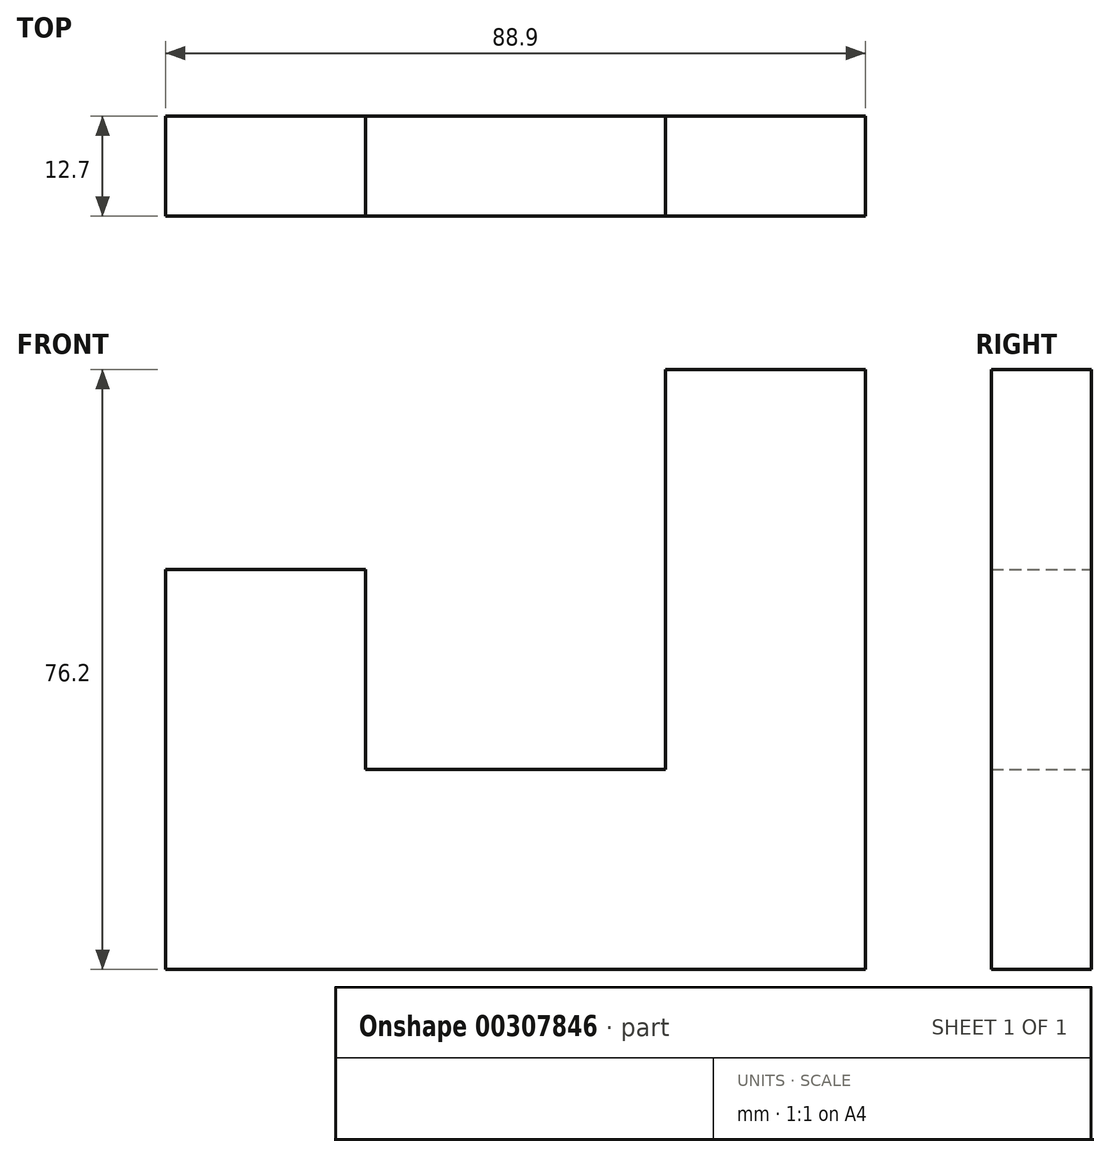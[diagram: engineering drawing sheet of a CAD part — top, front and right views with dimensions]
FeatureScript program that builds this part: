
annotation { "Feature Type Name" : "Feature", "Feature Type Description" : "" }
export const myFeature = defineFeature(function(context is Context, id is Id, definition is map)
    precondition{}
    {
        {
            var Q0;
            Q0=qCreatedBy(makeId("Front.planeOp"),FACE);
            var sketch = newSketch(context, id + "F0", { "sketchPlane" : qUnion([Q0])});
            skLineSegment(sketch, "E0", {"start": v(-35.1, -59.81) * mm, "end": v(53.8, -59.81) * mm});
            skLineSegment(sketch, "E1", {"start": v(53.8, -59.81) * mm, "end": v(53.8, 16.39) * mm});
            skLineSegment(sketch, "E2", {"start": v(53.8, 16.39) * mm, "end": v(28.4, 16.39) * mm});
            skLineSegment(sketch, "E3", {"start": v(28.4, 16.39) * mm, "end": v(28.4, -34.41) * mm});
            skLineSegment(sketch, "E4", {"start": v(28.4, -34.41) * mm, "end": v(-9.7, -34.41) * mm});
            skLineSegment(sketch, "E5", {"start": v(-9.7, -34.41) * mm, "end": v(-9.7, -9.01) * mm});
            skLineSegment(sketch, "E6", {"start": v(-9.7, -9.01) * mm, "end": v(-35.1, -9.01) * mm});
            skLineSegment(sketch, "E7", {"start": v(-35.1, -9.01) * mm, "end": v(-35.1, -59.81) * mm});
            skSolve(sketch);
        }
        {
            var Q0;
            Q0=makeQuery(id+"F0.imprint","IMPRINT",FACE,{"disambiguationData":[TD([[makeQuery(id+"F0.imprint","IMPRINT",EDGE,{"derivedFrom":sQuery(id+"F0.wireOp",EDGE,"E0")}),1.0]])]});
            extrude(context, id + "F1", {"entities" : qUnion([Q0]), "depth" : 12.7 * mm});
        }
    });
